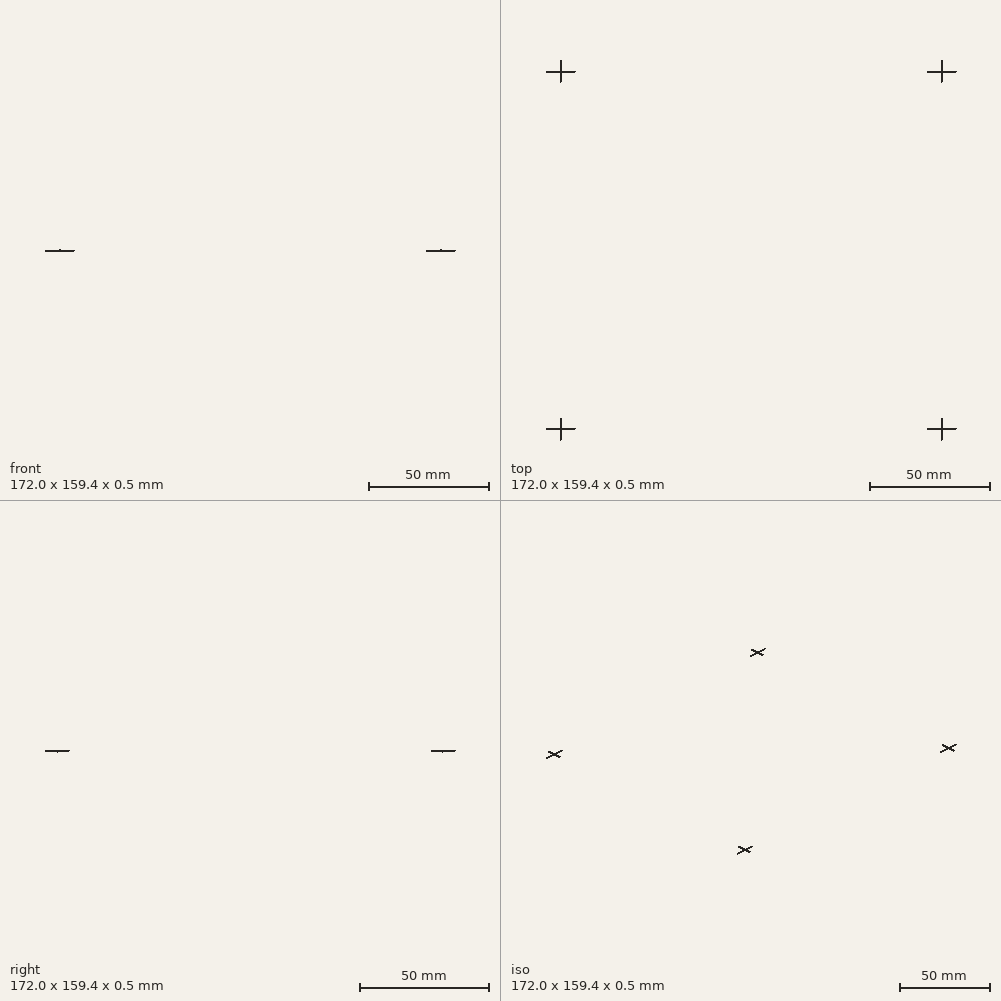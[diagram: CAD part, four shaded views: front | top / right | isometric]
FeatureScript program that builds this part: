
annotation { "Feature Type Name" : "Feature", "Feature Type Description" : "" }
export const myFeature = defineFeature(function(context is Context, id is Id, definition is map)
    precondition{}
    {
        {
            var Q0;
            Q0=qCreatedBy(makeId("Top.planeOp"),FACE);
            var sketch = newSketch(context, id + "F0", { "sketchPlane" : qUnion([Q0])});
            skLineSegment(sketch, "E0.bottom", {"start": v(-69.43, 39.73) * mm, "end": v(-57.43, 39.73) * mm});
            skLineSegment(sketch, "E0.top", {"start": v(-69.43, 39.3) * mm, "end": v(-57.43, 39.3) * mm});
            skLineSegment(sketch, "E0.left", {"start": v(-69.43, 39.73) * mm, "end": v(-69.43, 39.3) * mm});
            skLineSegment(sketch, "E0.right", {"start": v(-57.43, 39.73) * mm, "end": v(-57.43, 39.3) * mm});
            skLineSegment(sketch, "E1.bottom", {"start": v(-69.43, -110.27) * mm, "end": v(-57.43, -110.27) * mm});
            skLineSegment(sketch, "E1.top", {"start": v(-69.43, -110.7) * mm, "end": v(-57.43, -110.7) * mm});
            skLineSegment(sketch, "E1.left", {"start": v(-69.43, -110.27) * mm, "end": v(-69.43, -110.7) * mm});
            skLineSegment(sketch, "E1.right", {"start": v(-57.43, -110.27) * mm, "end": v(-57.43, -110.7) * mm});
            skLineSegment(sketch, "E2.bottom", {"start": v(90.57, 39.73) * mm, "end": v(102.57, 39.73) * mm});
            skLineSegment(sketch, "E2.top", {"start": v(90.57, 39.3) * mm, "end": v(102.57, 39.3) * mm});
            skLineSegment(sketch, "E2.left", {"start": v(90.57, 39.73) * mm, "end": v(90.57, 39.3) * mm});
            skLineSegment(sketch, "E2.right", {"start": v(102.57, 39.73) * mm, "end": v(102.57, 39.3) * mm});
            skLineSegment(sketch, "E3.bottom", {"start": v(90.57, -110.27) * mm, "end": v(102.57, -110.27) * mm});
            skLineSegment(sketch, "E3.top", {"start": v(90.57, -110.7) * mm, "end": v(102.57, -110.7) * mm});
            skLineSegment(sketch, "E3.left", {"start": v(90.57, -110.27) * mm, "end": v(90.57, -110.7) * mm});
            skLineSegment(sketch, "E3.right", {"start": v(102.57, -110.27) * mm, "end": v(102.57, -110.7) * mm});
            skPoint(sketch, "E4", {"position": v(-63.43, 39.73) * mm});
            skPoint(sketch, "E5", {"position": v(96.57, 39.73) * mm});
            skPoint(sketch, "E6", {"position": v(-69.43, 39.52) * mm});
            skPoint(sketch, "E7", {"position": v(-69.43, -110.48) * mm});
            skSolve(sketch);
        }
        {
            var Q0;
            Q0 = qSketchRegion(id + "F0", true);
            extrude(context, id + "F1", {"entities" : qUnion([Q0]), "depth" : 0.3 * mm, "offsetDistance" : 25 * mm});
        }
        {
            var Q0;
            Q0=qCreatedBy(makeId("Top.planeOp"),FACE);
            cPlane(context, id + "F2", {"entities" : qUnion([Q0]), "cplaneType" : CPlaneType.OFFSET, "offset" : 0.3 * mm, "width" : 150 * mm, "height" : 150 * mm});
        }
        {
            var Q0;
            Q0=qCreatedBy(id+"F2.planeOp",FACE);
            var sketch = newSketch(context, id + "F3", { "sketchPlane" : qUnion([Q0])});
            skLineSegment(sketch, "E8.bottom", {"start": v(-63.63, 44.22) * mm, "end": v(-63.22, 44.22) * mm});
            skLineSegment(sketch, "E8.top", {"start": v(-63.63, 34.82) * mm, "end": v(-63.22, 34.82) * mm});
            skLineSegment(sketch, "E8.left", {"start": v(-63.63, 44.22) * mm, "end": v(-63.63, 34.82) * mm});
            skLineSegment(sketch, "E8.right", {"start": v(-63.22, 44.22) * mm, "end": v(-63.22, 34.82) * mm});
            skLineSegment(sketch, "E9.bottom", {"start": v(-63.63, -105.78) * mm, "end": v(-63.22, -105.78) * mm});
            skLineSegment(sketch, "E9.top", {"start": v(-63.63, -115.18) * mm, "end": v(-63.22, -115.18) * mm});
            skLineSegment(sketch, "E9.left", {"start": v(-63.63, -105.78) * mm, "end": v(-63.63, -115.18) * mm});
            skLineSegment(sketch, "E9.right", {"start": v(-63.22, -105.78) * mm, "end": v(-63.22, -115.18) * mm});
            skLineSegment(sketch, "E10.bottom", {"start": v(96.37, -105.78) * mm, "end": v(96.78, -105.78) * mm});
            skLineSegment(sketch, "E10.top", {"start": v(96.37, -115.18) * mm, "end": v(96.78, -115.18) * mm});
            skLineSegment(sketch, "E10.left", {"start": v(96.37, -105.78) * mm, "end": v(96.37, -115.18) * mm});
            skLineSegment(sketch, "E10.right", {"start": v(96.78, -105.78) * mm, "end": v(96.78, -115.18) * mm});
            skLineSegment(sketch, "E11.bottom", {"start": v(96.37, 44.22) * mm, "end": v(96.78, 44.22) * mm});
            skLineSegment(sketch, "E11.top", {"start": v(96.37, 34.82) * mm, "end": v(96.78, 34.82) * mm});
            skLineSegment(sketch, "E11.left", {"start": v(96.37, 44.22) * mm, "end": v(96.37, 34.82) * mm});
            skLineSegment(sketch, "E11.right", {"start": v(96.78, 44.22) * mm, "end": v(96.78, 34.82) * mm});
            skLineSegment(sketch, "E12", {"start": v(-63.63, 44.22) * mm, "end": v(-63.22, 34.82) * mm, "construction": true});
            skPoint(sketch, "E13", {"position": v(-63.43, 39.52) * mm});
            skLineSegment(sketch, "E14.0.0", {"start": v(-69.43, 39.73) * mm, "end": v(-69.43, 39.3) * mm, "construction": true});
            skLineSegment(sketch, "E14.0.1", {"start": v(-69.43, 39.3) * mm, "end": v(-57.43, 39.3) * mm, "construction": true});
            skLineSegment(sketch, "E14.0.2", {"start": v(-57.43, 39.3) * mm, "end": v(-57.43, 39.73) * mm, "construction": true});
            skLineSegment(sketch, "E14.0.3", {"start": v(-57.43, 39.73) * mm, "end": v(-69.43, 39.73) * mm, "construction": true});
            skLineSegment(sketch, "E15", {"start": v(-69.43, 39.73) * mm, "end": v(-57.43, 39.3) * mm, "construction": true});
            skLineSegment(sketch, "E16.0.0", {"start": v(90.57, 39.73) * mm, "end": v(90.57, 39.3) * mm, "construction": true});
            skLineSegment(sketch, "E16.0.1", {"start": v(90.57, 39.3) * mm, "end": v(102.57, 39.3) * mm, "construction": true});
            skLineSegment(sketch, "E16.0.2", {"start": v(102.57, 39.3) * mm, "end": v(102.57, 39.73) * mm, "construction": true});
            skLineSegment(sketch, "E16.0.3", {"start": v(102.57, 39.73) * mm, "end": v(90.57, 39.73) * mm, "construction": true});
            skLineSegment(sketch, "E17", {"start": v(90.57, 39.73) * mm, "end": v(102.57, 39.3) * mm, "construction": true});
            skPoint(sketch, "E18", {"position": v(96.57, 39.52) * mm});
            skLineSegment(sketch, "E19", {"start": v(96.37, 44.22) * mm, "end": v(96.78, 34.82) * mm, "construction": true});
            skLineSegment(sketch, "E20", {"start": v(96.37, -105.78) * mm, "end": v(96.78, -115.18) * mm, "construction": true});
            skPoint(sketch, "E21", {"position": v(96.57, -110.48) * mm});
            skLineSegment(sketch, "E22.0.0", {"start": v(90.57, -110.27) * mm, "end": v(90.57, -110.7) * mm, "construction": true});
            skLineSegment(sketch, "E22.0.1", {"start": v(90.57, -110.7) * mm, "end": v(102.57, -110.7) * mm, "construction": true});
            skLineSegment(sketch, "E22.0.2", {"start": v(102.57, -110.7) * mm, "end": v(102.57, -110.27) * mm, "construction": true});
            skLineSegment(sketch, "E22.0.3", {"start": v(102.57, -110.27) * mm, "end": v(90.57, -110.27) * mm, "construction": true});
            skLineSegment(sketch, "E23", {"start": v(90.57, -110.27) * mm, "end": v(102.57, -110.7) * mm, "construction": true});
            skSolve(sketch);
        }
        {
            var Q0;
            Q0 = qSketchRegion(id + "F3", true);
            extrude(context, id + "F4", {"entities" : qUnion([Q0]), "depth" : 0.2 * mm, "offsetDistance" : 25 * mm});
        }
    });
